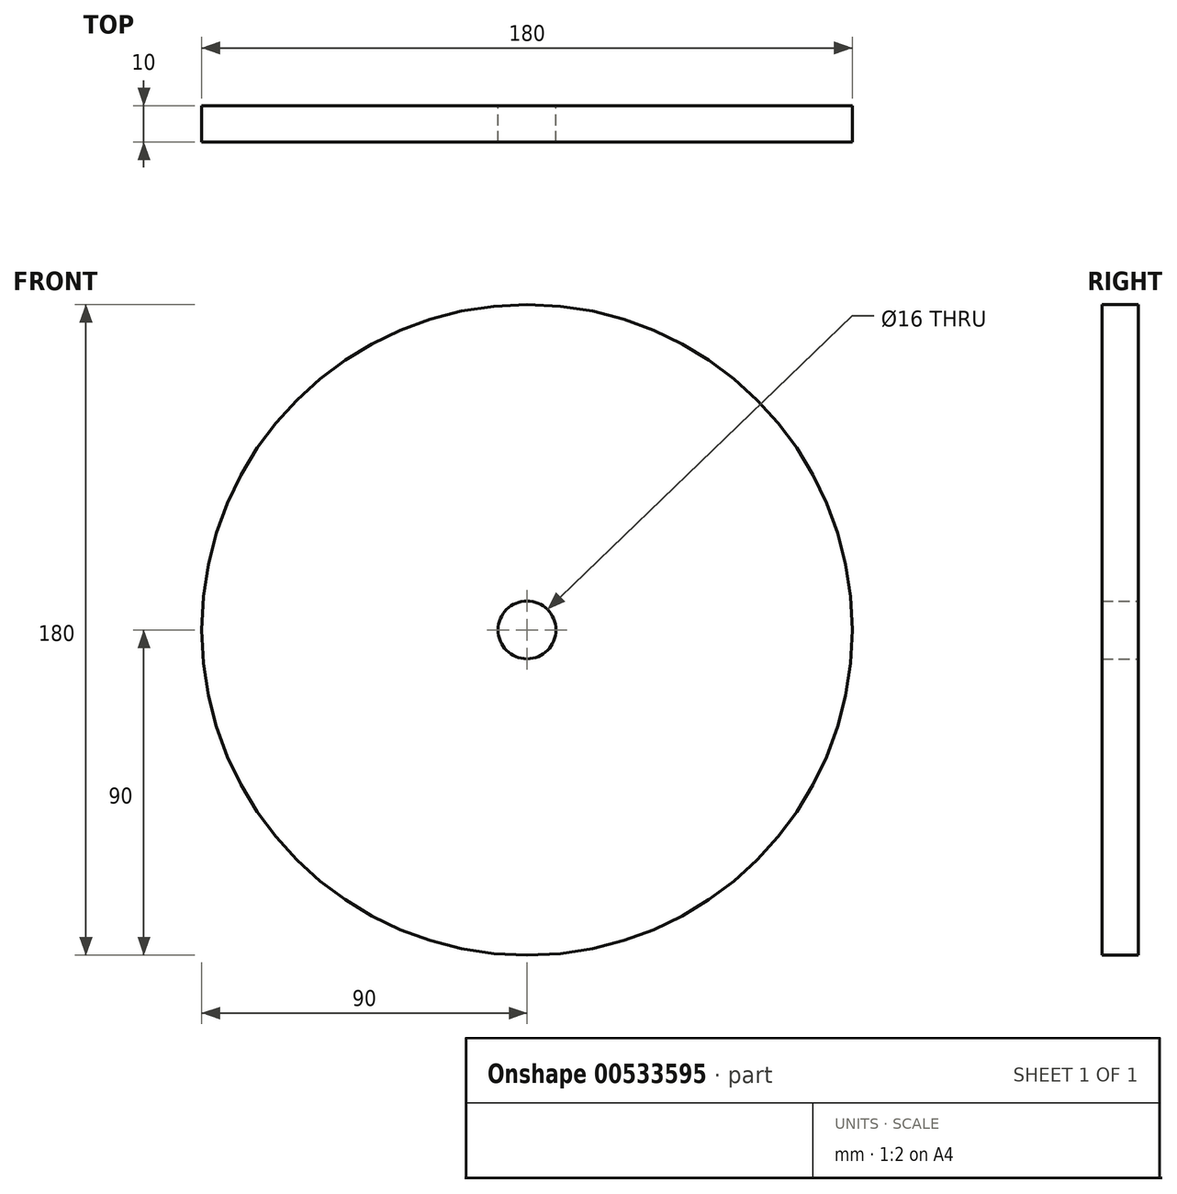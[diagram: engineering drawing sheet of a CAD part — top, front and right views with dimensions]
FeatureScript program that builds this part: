
annotation { "Feature Type Name" : "Feature", "Feature Type Description" : "" }
export const myFeature = defineFeature(function(context is Context, id is Id, definition is map)
    precondition{}
    {
        {
            var Q0;
            Q0=qCreatedBy(makeId("Front.planeOp"),FACE);
            var sketch = newSketch(context, id + "F0", { "sketchPlane" : qUnion([Q0])});
            skCircle(sketch, "E0", {"center": v(0, 0) * mm, "radius": 90 * mm});
            skCircle(sketch, "E1", {"center": v(0, 0) * mm, "radius": 8 * mm});
            skSolve(sketch);
        }
        {
            var Q0;
            Q0=qSketchRegion(id+"F0",true);
            extrude(context, id + "F1", {"entities" : qUnion([Q0]), "depth" : 10 * mm});
        }
    });
